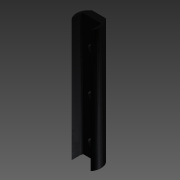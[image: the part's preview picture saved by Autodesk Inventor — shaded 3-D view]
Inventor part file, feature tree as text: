
AUTODESK INVENTOR PART (.ipt)
format: ipt  version: 2015 (Build 190159000, 159)  size: 117,248 bytes
history: native  units: mm
features: sketch x3, extrude x2, other x1, hole x1
ambient origin geometry x8: Origin, YZ Plane, XZ Plane, XY Plane, X Axis, Y Axis, Z Axis, Center Point
bodies: Body1 (feature_tree)
feature tree (7):
  other  "Bryła1"
  extrude  "Wyciągnięcie proste1"  Depth=18.0mm
  extrude  "Wyciągnięcie proste2"  Depth=90.0mm TaperAngle=0.0deg
  hole  "Otwór1"  [1 undecoded]
  sketch  "Szkic1"
  sketch  "Szkic2"
  sketch  "Szkic3"
note: 1 required parameter value undecoded (feature->parameter linkage not recoverable at this tier; creation-order binding heuristic only, values carry confidence <= 0.55)
